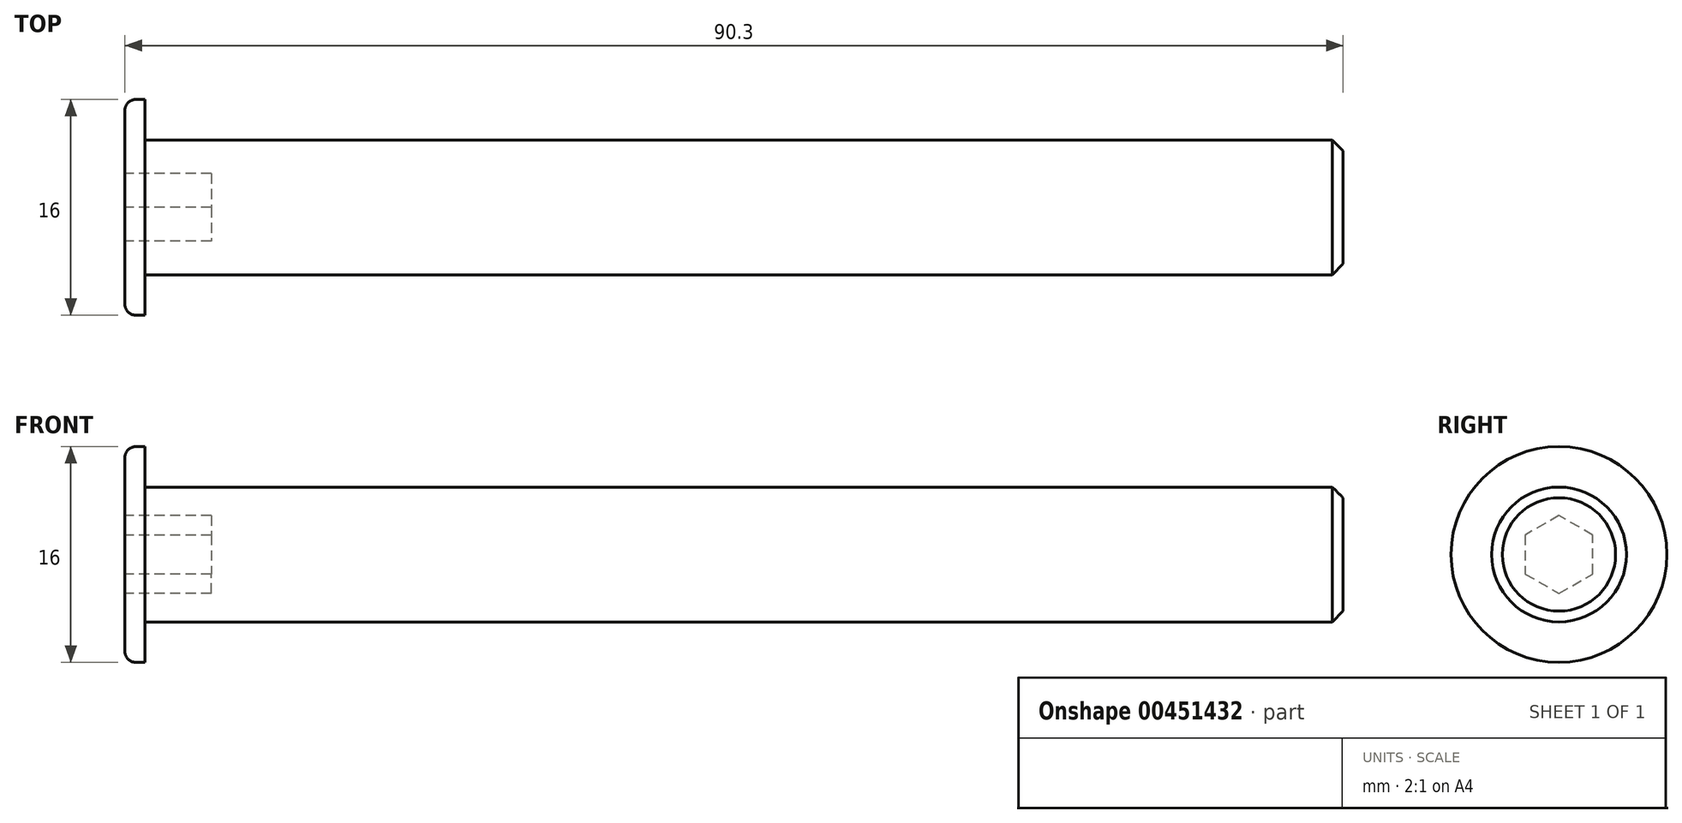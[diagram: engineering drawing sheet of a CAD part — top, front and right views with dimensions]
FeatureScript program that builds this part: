
annotation { "Feature Type Name" : "Feature", "Feature Type Description" : "" }
export const myFeature = defineFeature(function(context is Context, id is Id, definition is map)
    precondition{}
    {
        {
            var Q0;
            Q0=qCreatedBy(makeId("Top.planeOp"),FACE);
            var sketch = newSketch(context, id + "F0", { "sketchPlane" : qUnion([Q0])});
            skLineSegment(sketch, "E0", {"start": v(0, 0) * mm, "end": v(90.3, 0) * mm});
            skLineSegment(sketch, "E1", {"start": v(90.3, 0) * mm, "end": v(90.3, -5) * mm});
            skLineSegment(sketch, "E2", {"start": v(90.3, -5) * mm, "end": v(1.5, -5) * mm});
            skLineSegment(sketch, "E3", {"start": v(1.5, -5) * mm, "end": v(1.5, -8) * mm});
            skLineSegment(sketch, "E4", {"start": v(1.5, -8) * mm, "end": v(0, -8) * mm});
            skLineSegment(sketch, "E5", {"start": v(0, -8) * mm, "end": v(0, 0) * mm});
            skSolve(sketch);
        }
        {
            var Q0;
            Q0=qSketchRegion(id+"F0",true);
            var Q1;
            Q1=sQuery(id+"F0.wireOp",EDGE,"E0");
            revolve(context, id + "F1", {"entities" : qUnion([Q0]), "axis" : qUnion([Q1]), "revolveType" : RevolveType.FULL});
        }
        {
            var Q0;
            Q0=makeQuery(id+"F1.opRevolve","SWEPT_EDGE",EDGE,{"disambiguationData":[OSD([sQuery(id+"F0.wireOp",EDGE,"E1"),sQuery(id+"F0.wireOp",EDGE,"E2")])]});
            chamfer(context, id + "F2", {"entities" : qUnion([Q0]), "chamferType" : ChamferType.OFFSET_ANGLE, "width" : .80 * mm, "oppositeDirection" : false, "angle" : 45 * degree, "tangentPropagation" : true});
        }
        {
            var Q0;
            Q0=makeQuery(id+"F1.opRevolve","SWEPT_EDGE",EDGE,{"disambiguationData":[OSD([sQuery(id+"F0.wireOp",EDGE,"E4"),sQuery(id+"F0.wireOp",EDGE,"E5")])]});
            fillet(context, id + "F3", {"entities" : qUnion([Q0]), "radius" : 0.8 * mm, "tangentPropagation" : true, "allowEdgeOverflow" : false});
        }
        {
            var Q0;
            Q0=makeQuery(id+"F1.opRevolve","SWEPT_FACE",FACE,{"disambiguationData":[OSD([sQuery(id+"F0.wireOp",EDGE,"E5")])]});
            var sketch = newSketch(context, id + "F4", { "sketchPlane" : qUnion([Q0])});
            skCircle(sketch, "E6.cCircle", {"center": v(0, 0) * mm, "radius": 2.5 * mm, "construction": true});
            skLineSegment(sketch, "E6.0", {"start": v(2.5, 1.44) * mm, "end": v(2.5, -1.44) * mm});
            skLineSegment(sketch, "E6.1", {"start": v(2.5, -1.44) * mm, "end": v(0, -2.89) * mm});
            skLineSegment(sketch, "E6.2", {"start": v(0, -2.9) * mm, "end": v(-2.5, -1.45) * mm});
            skLineSegment(sketch, "E6.3", {"start": v(-2.5, -1.45) * mm, "end": v(-2.5, 1.44) * mm});
            skLineSegment(sketch, "E6.4", {"start": v(-2.5, 1.44) * mm, "end": v(0, 2.89) * mm});
            skLineSegment(sketch, "E6.5", {"start": v(0, 2.9) * mm, "end": v(2.5, 1.44) * mm});
            skPoint(sketch, "E6.0.midPoint", {"position": v(2.5, 0) * mm});
            skSolve(sketch);
        }
        {
            var Q0;
            Q0=qSketchRegion(id+"F4",true);
            extrude(context, id + "F5", {"entities" : qUnion([Q0]), "operationType" : NewBodyOperationType.REMOVE, "oppositeDirection" : true, "depth" : 6.4 * mm});
        }
    });
